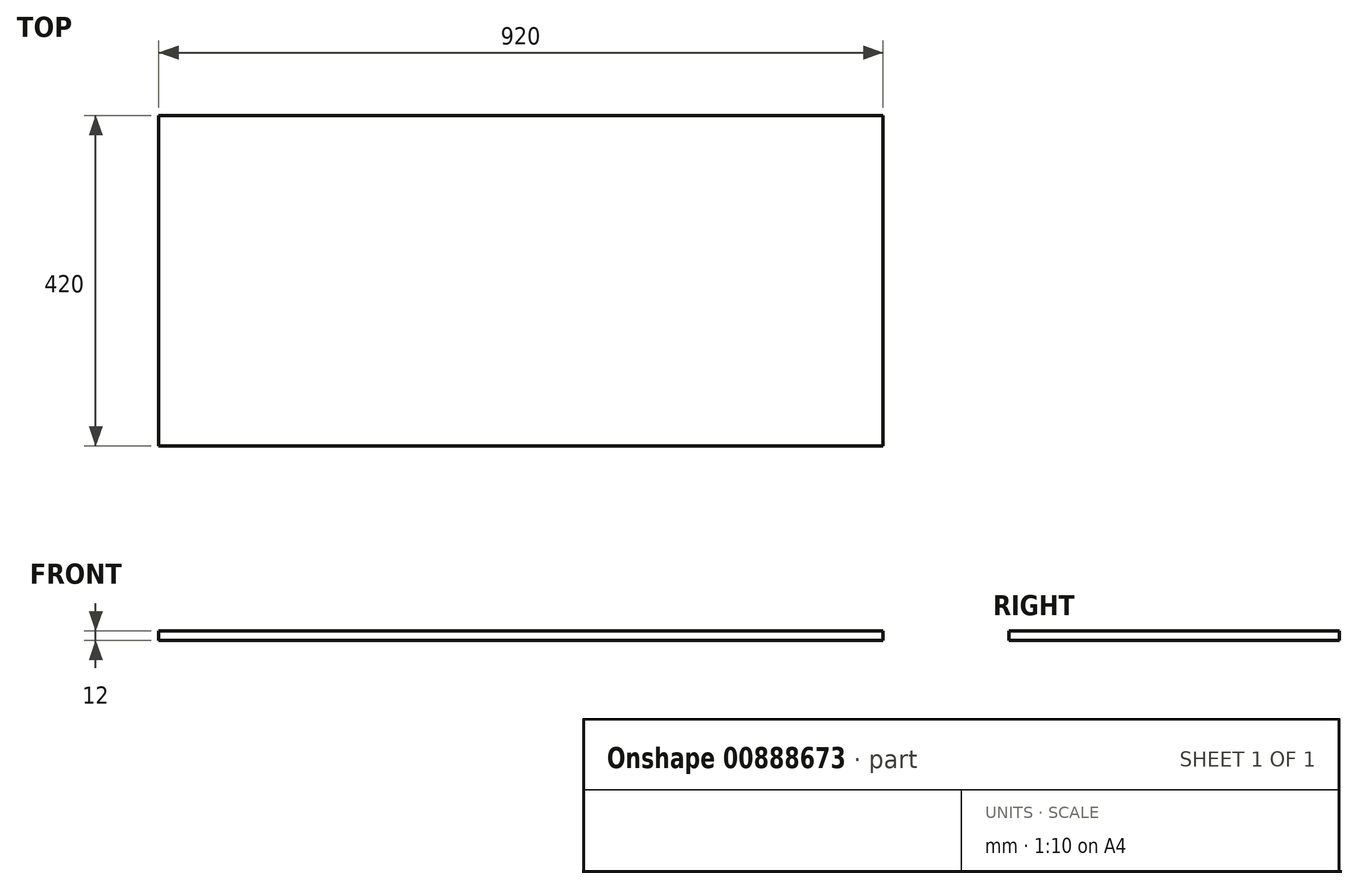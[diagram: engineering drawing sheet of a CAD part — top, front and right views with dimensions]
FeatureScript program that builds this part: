
annotation { "Feature Type Name" : "Feature", "Feature Type Description" : "" }
export const myFeature = defineFeature(function(context is Context, id is Id, definition is map)
    precondition{}
    {
        {
            var Q0;
            Q0=qCreatedBy(makeId("Top.planeOp"),FACE);
            var sketch = newSketch(context, id + "F0", { "sketchPlane" : qUnion([Q0])});
            skLineSegment(sketch, "E0.bottom", {"start": v(-460, -210) * mm, "end": v(460, -210) * mm});
            skLineSegment(sketch, "E0.top", {"start": v(-460, 210) * mm, "end": v(460, 210) * mm});
            skLineSegment(sketch, "E0.left", {"start": v(-460, -210) * mm, "end": v(-460, 210) * mm});
            skLineSegment(sketch, "E0.right", {"start": v(460, -210) * mm, "end": v(460, 210) * mm});
            skSolve(sketch);
        }
        {
            var Q0;
            Q0 = qSketchRegion(id + "F0", true);
            extrude(context, id + "F1", {"entities" : qUnion([Q0]), "depth" : 6 * mm, "offsetDistance" : 25 * mm, "hasSecondDirection" : true, "secondDirectionOppositeDirection" : true, "secondDirectionDepth" : 6 * mm});
        }
    });
